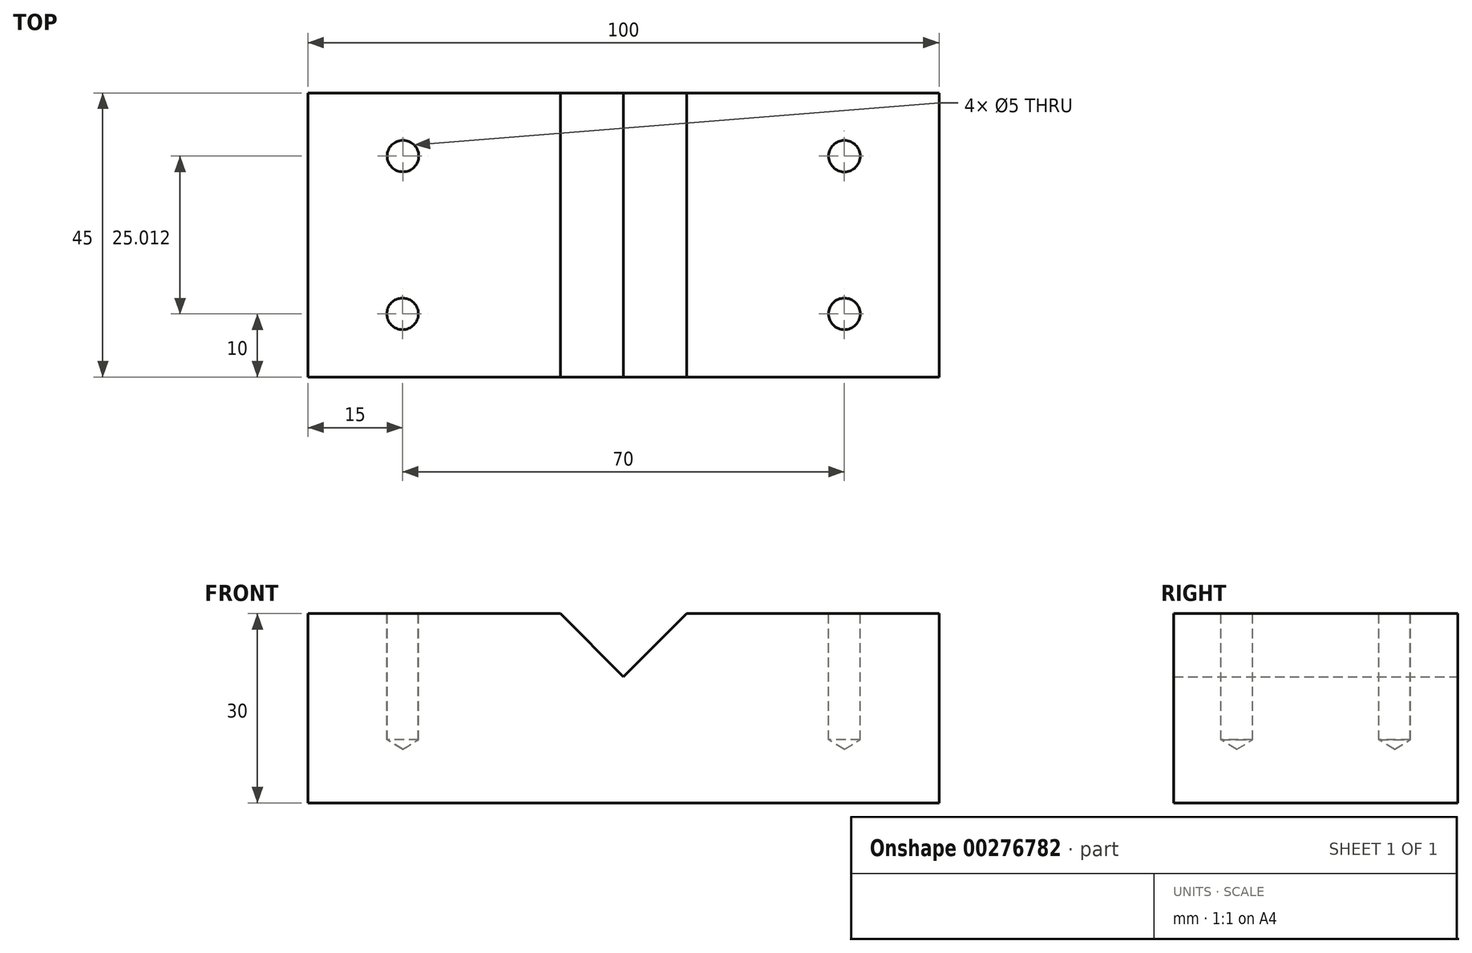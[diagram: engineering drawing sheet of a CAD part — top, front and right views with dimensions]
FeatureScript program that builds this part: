
annotation { "Feature Type Name" : "Feature", "Feature Type Description" : "" }
export const myFeature = defineFeature(function(context is Context, id is Id, definition is map)
    precondition{}
    {
        {
            var Q0;
            Q0=qCreatedBy(makeId("Front.planeOp"),FACE);
            var sketch = newSketch(context, id + "F0", { "sketchPlane" : qUnion([Q0])});
            skPoint(sketch, "E0.middle", {"position": v(0, 0) * mm});
            skLineSegment(sketch, "E1", {"start": v(20, 20) * mm, "end": v(50, 20) * mm});
            skLineSegment(sketch, "E2", {"start": v(50, 20) * mm, "end": v(50, 0) * mm});
            skLineSegment(sketch, "E3", {"start": v(-20, 20) * mm, "end": v(-50, 20) * mm});
            skLineSegment(sketch, "E4", {"start": v(-50, 20) * mm, "end": v(-50, 0) * mm});
            skLineSegment(sketch, "E5", {"start": v(-50, 0) * mm, "end": v(-50, -10) * mm});
            skLineSegment(sketch, "E6", {"start": v(-50, -10) * mm, "end": v(50, -10) * mm});
            skLineSegment(sketch, "E7", {"start": v(50, -10) * mm, "end": v(50, 0) * mm});
            skLineSegment(sketch, "E8", {"start": v(-20, 20) * mm, "end": v(-10, 20) * mm});
            skLineSegment(sketch, "E9", {"start": v(20, 20) * mm, "end": v(10, 20) * mm});
            skLineSegment(sketch, "E10", {"start": v(10, 20) * mm, "end": v(0, 10) * mm});
            skLineSegment(sketch, "E11", {"start": v(-10, 20) * mm, "end": v(0, 10) * mm});
            skSolve(sketch);
        }
        {
            var Q0;
            Q0=qSketchRegion(id+"F0",true);
            extrude(context, id + "F1", {"entities" : qUnion([Q0]), "depth" : 45 * mm});
        }
        {
            var Q0;
            Q0=makeQuery(id+"F1.opExtrude","SWEPT_FACE",FACE,{"disambiguationData":[OSD([sQuery(id+"F0.wireOp",EDGE,"E1")])]});
            var sketch = newSketch(context, id + "F2", { "sketchPlane" : qUnion([Q0])});
            skCircle(sketch, "E12", {"center": v(35, -35) * mm, "radius": 2 * mm});
            skSolve(sketch);
        }
        {
            var Q0;
            Q0=sQuery(id+"F2.wireOp",VERTEX,"E12.center");
            var Q1;
            Q1=makeQuery(id+"F1.opExtrude","SWEPT_BODY",BODY,{"disambiguationData":[OSD([sQuery(id+"F0.wireOp",EDGE,"76PpERGf-RPlK-5DYp-Uilo-4EMAaiWrKBhD"),sQuery(id+"F0.wireOp",EDGE,"PzodHsil-XRGJ-AnxR-qKlP-lsXBW81SyEPC"),sQuery(id+"F0.wireOp",EDGE,"E1"),sQuery(id+"F0.wireOp",EDGE,"E2"),sQuery(id+"F0.wireOp",EDGE,"E3"),sQuery(id+"F0.wireOp",EDGE,"E4"),sQuery(id+"F0.wireOp",EDGE,"E5"),sQuery(id+"F0.wireOp",EDGE,"E6"),sQuery(id+"F0.wireOp",EDGE,"E7")])]});
            hole(context, id + "F3", {"style" : HoleStyle.SIMPLE, "endStyle" : HoleEndStyle.BLIND, "holeDiameter" : 5 * mm, "holeDepth" : 20 * mm, "tappedDepth" : 12.7 * mm, "tapClearance" : 3, "locations" : qUnion([Q0]), "scope" : qUnion([Q1])});
        }
        {
            var Q0;
            Q0=makeQuery(id+"F1.opExtrude","SWEPT_FACE",FACE,{"disambiguationData":[OSD([sQuery(id+"F0.wireOp",EDGE,"E1")])]});
            var sketch = newSketch(context, id + "F4", { "sketchPlane" : qUnion([Q0])});
            skCircle(sketch, "E13", {"center": v(35, -10) * mm, "radius": 2 * mm});
            skSolve(sketch);
        }
        {
            var Q0;
            Q0=sQuery(id+"F4.wireOp",VERTEX,"E13.center");
            var Q1;
            Q1=makeQuery(id+"F1.opExtrude","SWEPT_BODY",BODY,{"disambiguationData":[OSD([sQuery(id+"F0.wireOp",EDGE,"76PpERGf-RPlK-5DYp-Uilo-4EMAaiWrKBhD"),sQuery(id+"F0.wireOp",EDGE,"PzodHsil-XRGJ-AnxR-qKlP-lsXBW81SyEPC"),sQuery(id+"F0.wireOp",EDGE,"E1"),sQuery(id+"F0.wireOp",EDGE,"E2"),sQuery(id+"F0.wireOp",EDGE,"E3"),sQuery(id+"F0.wireOp",EDGE,"E4"),sQuery(id+"F0.wireOp",EDGE,"E5"),sQuery(id+"F0.wireOp",EDGE,"E6"),sQuery(id+"F0.wireOp",EDGE,"E7")])]});
            hole(context, id + "F5", {"style" : HoleStyle.SIMPLE, "endStyle" : HoleEndStyle.BLIND, "holeDiameter" : 5 * mm, "holeDepth" : 20 * mm, "tappedDepth" : 12.7 * mm, "tapClearance" : 3, "locations" : qUnion([Q0]), "scope" : qUnion([Q1])});
        }
        {
            var Q0;
            Q0=makeQuery(id+"F1.opExtrude","SWEPT_FACE",FACE,{"disambiguationData":[OSD([sQuery(id+"F0.wireOp",EDGE,"E3")])]});
            var sketch = newSketch(context, id + "F6", { "sketchPlane" : qUnion([Q0])});
            skCircle(sketch, "E14", {"center": v(-35, -10) * mm, "radius": 2 * mm});
            skSolve(sketch);
        }
        {
            var Q0;
            Q0=makeQuery(id+"F1.opExtrude","SWEPT_FACE",FACE,{"disambiguationData":[OSD([sQuery(id+"F0.wireOp",EDGE,"E3")])]});
            var sketch = newSketch(context, id + "F7", { "sketchPlane" : qUnion([Q0])});
            skCircle(sketch, "E15", {"center": v(-35, -35) * mm, "radius": 2 * mm});
            skSolve(sketch);
        }
        {
            var Q0;
            Q0=sQuery(id+"F7.wireOp",VERTEX,"E15.center");
            var Q1;
            Q1=makeQuery(id+"F1.opExtrude","SWEPT_BODY",BODY,{"disambiguationData":[OSD([sQuery(id+"F0.wireOp",EDGE,"76PpERGf-RPlK-5DYp-Uilo-4EMAaiWrKBhD"),sQuery(id+"F0.wireOp",EDGE,"PzodHsil-XRGJ-AnxR-qKlP-lsXBW81SyEPC"),sQuery(id+"F0.wireOp",EDGE,"E1"),sQuery(id+"F0.wireOp",EDGE,"E2"),sQuery(id+"F0.wireOp",EDGE,"E3"),sQuery(id+"F0.wireOp",EDGE,"E4"),sQuery(id+"F0.wireOp",EDGE,"E5"),sQuery(id+"F0.wireOp",EDGE,"E6"),sQuery(id+"F0.wireOp",EDGE,"E7")])]});
            hole(context, id + "F8", {"style" : HoleStyle.SIMPLE, "endStyle" : HoleEndStyle.BLIND, "holeDiameter" : 5 * mm, "holeDepth" : 20 * mm, "tappedDepth" : 12.7 * mm, "tapClearance" : 3, "locations" : qUnion([Q0]), "scope" : qUnion([Q1])});
        }
        {
            var Q0;
            Q0=makeQuery(id+"F6.imprint","IMPRINT",FACE,{"disambiguationData":[TD([[makeQuery(id+"F6.imprint","IMPRINT",EDGE,{"derivedFrom":sQuery(id+"F6.wireOp",EDGE,"E14")}),-1.0]])]});
            var sketch = newSketch(context, id + "F9", { "sketchPlane" : qUnion([Q0])});
            skCircle(sketch, "E16", {"center": v(-34.95, -9.99) * mm, "radius": 2.5 * mm});
            skSolve(sketch);
        }
        {
            var Q0;
            Q0=sQuery(id+"F9.wireOp",VERTEX,"E16.center");
            var Q1;
            Q1=makeQuery(id+"F1.opExtrude","SWEPT_BODY",BODY,{"disambiguationData":[OSD([sQuery(id+"F0.wireOp",EDGE,"E1"),sQuery(id+"F0.wireOp",EDGE,"E2"),sQuery(id+"F0.wireOp",EDGE,"E3"),sQuery(id+"F0.wireOp",EDGE,"E4"),sQuery(id+"F0.wireOp",EDGE,"E5"),sQuery(id+"F0.wireOp",EDGE,"E6"),sQuery(id+"F0.wireOp",EDGE,"E7"),sQuery(id+"F0.wireOp",EDGE,"E8"),sQuery(id+"F0.wireOp",EDGE,"E9"),sQuery(id+"F0.wireOp",EDGE,"E10"),sQuery(id+"F0.wireOp",EDGE,"E11")])]});
            hole(context, id + "F10", {"style" : HoleStyle.SIMPLE, "endStyle" : HoleEndStyle.BLIND, "holeDiameter" : 5 * mm, "holeDepth" : 20 * mm, "tappedDepth" : 12.7 * mm, "tapClearance" : 3, "locations" : qUnion([Q0]), "scope" : qUnion([Q1])});
        }
    });
